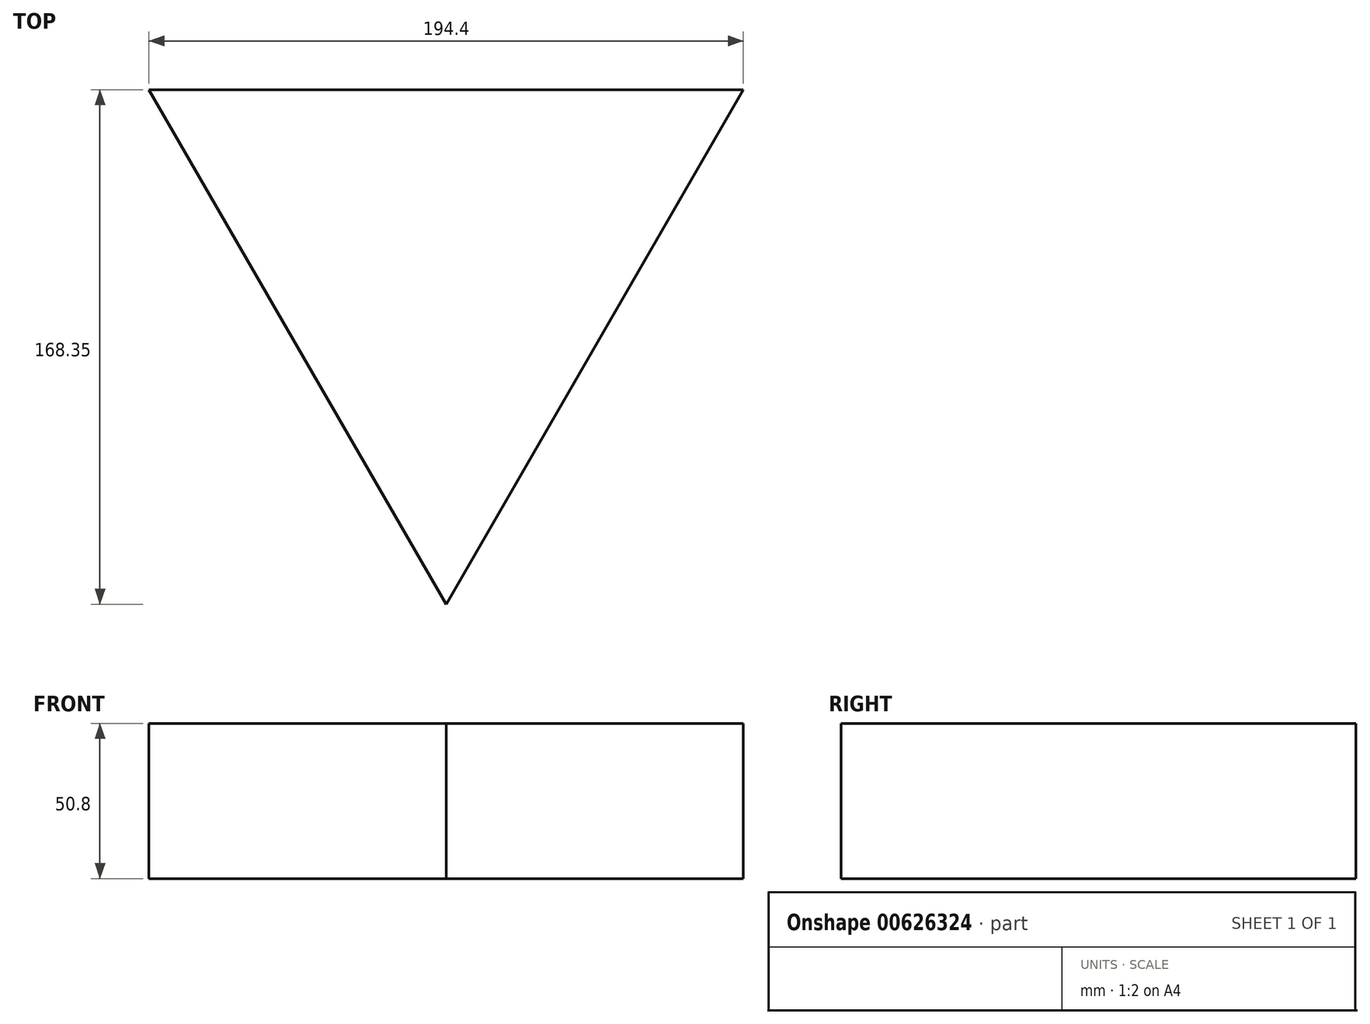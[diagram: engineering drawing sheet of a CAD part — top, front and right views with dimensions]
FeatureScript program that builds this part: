
annotation { "Feature Type Name" : "Feature", "Feature Type Description" : "" }
export const myFeature = defineFeature(function(context is Context, id is Id, definition is map)
    precondition{}
    {
        {
            var Q0;
            Q0=qCreatedBy(makeId("Top.planeOp"),FACE);
            var sketch = newSketch(context, id + "F0", { "sketchPlane" : qUnion([Q0])});
            skCircle(sketch, "E0.cCircle", {"center": v(0, 0) * mm, "radius": 56.12 * mm, "construction": true});
            skLineSegment(sketch, "E0.0", {"start": v(-97.2, 56.12) * mm, "end": v(97.2, 56.12) * mm});
            skLineSegment(sketch, "E0.1", {"start": v(97.2, 56.12) * mm, "end": v(0, -112.23) * mm});
            skLineSegment(sketch, "E0.2", {"start": v(0, -112.23) * mm, "end": v(-97.2, 56.12) * mm});
            skPoint(sketch, "E0.0.midPoint", {"position": v(0, 56.12) * mm});
            skSolve(sketch);
        }
        {
            var Q0;
            Q0=makeQuery(id+"F0.imprint","IMPRINT",FACE,{"disambiguationData":[TD([[makeQuery(id+"F0.imprint","IMPRINT",EDGE,{"derivedFrom":sQuery(id+"F0.wireOp",EDGE,"E0.0")}),-1.0]])]});
            extrude(context, id + "F1", {"entities" : qUnion([Q0]), "depth" : 50.8 * mm, "offsetDistance" : 25.4 * mm});
        }
    });
